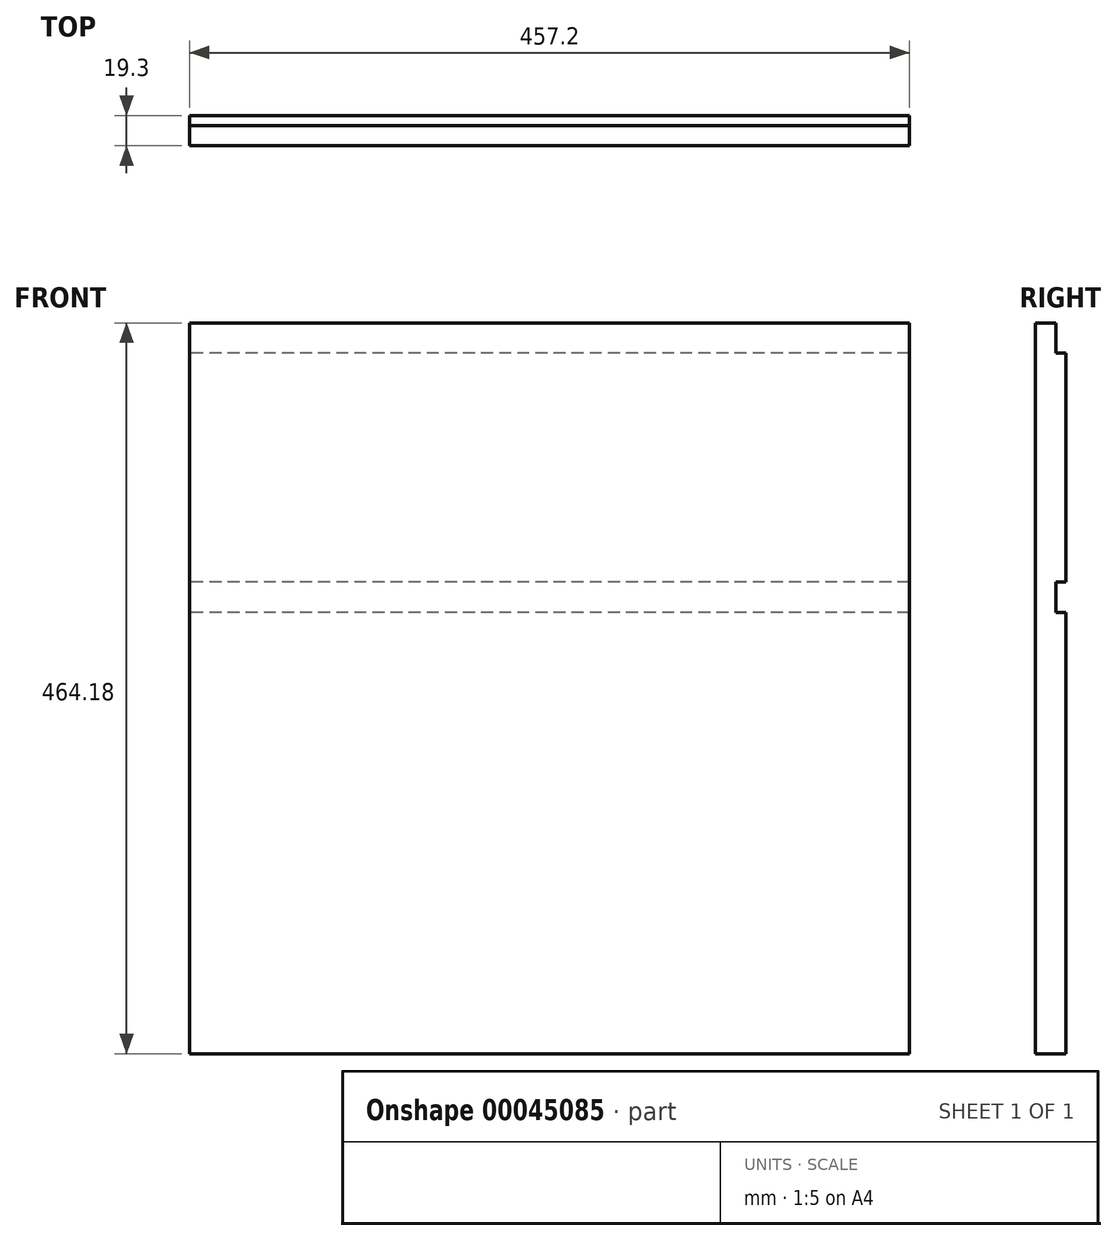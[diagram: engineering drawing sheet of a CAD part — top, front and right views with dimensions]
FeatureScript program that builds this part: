
annotation { "Feature Type Name" : "Feature", "Feature Type Description" : "" }
export const myFeature = defineFeature(function(context is Context, id is Id, definition is map)
    precondition{}
    {
        {
            var Q0;
            Q0=qCreatedBy(makeId("Front.planeOp"),FACE);
            var sketch = newSketch(context, id + "F0", { "sketchPlane" : qUnion([Q0])});
            skLineSegment(sketch, "E0.rect.bottom", {"start": v(-228.6, 232.1) * mm, "end": v(228.6, 232.1) * mm});
            skLineSegment(sketch, "E0.rect.top", {"start": v(-228.6, -232.1) * mm, "end": v(228.6, -232.1) * mm});
            skLineSegment(sketch, "E0.rect.left", {"start": v(-228.6, 232.1) * mm, "end": v(-228.6, -232.1) * mm});
            skLineSegment(sketch, "E0.rect.right", {"start": v(228.6, 232.1) * mm, "end": v(228.6, -232.1) * mm});
            skPoint(sketch, "E0.rect.middle", {"position": v(0, 0) * mm});
            skSolve(sketch);
        }
        {
            var Q0;
            Q0 = qSketchRegion(id + "F0", true);
            extrude(context, id + "F1", {"entities" : qUnion([Q0]), "depth" : 19.3 * mm});
        }
        {
            var Q0;
            Q0=makeQuery(id+"F1.opExtrude","CAP_FACE",FACE,{"disambiguationData":[OSD([sQuery(id+"F0.wireOp",EDGE,"E0.rect.bottom"),sQuery(id+"F0.wireOp",EDGE,"E0.rect.top"),sQuery(id+"F0.wireOp",EDGE,"E0.rect.left"),sQuery(id+"F0.wireOp",EDGE,"E0.rect.right")])],"isStart":true});
            var sketch = newSketch(context, id + "F2", { "sketchPlane" : qUnion([Q0])});
            skLineSegment(sketch, "E1.bottom", {"start": v(-228.6, 232.1) * mm, "end": v(228.6, 232.1) * mm});
            skLineSegment(sketch, "E1.top", {"start": v(-228.6, 212.79) * mm, "end": v(228.6, 212.79) * mm});
            skLineSegment(sketch, "E1.left", {"start": v(-228.6, 232.1) * mm, "end": v(-228.6, 212.79) * mm});
            skLineSegment(sketch, "E1.right", {"start": v(228.6, 232.1) * mm, "end": v(228.6, 212.79) * mm});
            skLineSegment(sketch, "E2.bottom", {"start": v(-228.6, 67.37) * mm, "end": v(228.6, 67.37) * mm});
            skLineSegment(sketch, "E2.top", {"start": v(-228.6, 48.07) * mm, "end": v(228.6, 48.07) * mm});
            skLineSegment(sketch, "E2.left", {"start": v(-228.6, 67.37) * mm, "end": v(-228.6, 48.07) * mm});
            skLineSegment(sketch, "E2.right", {"start": v(228.6, 67.37) * mm, "end": v(228.6, 48.07) * mm});
            skSolve(sketch);
        }
        {
            var Q0;
            Q0 = qSketchRegion(id + "F2", true);
            extrude(context, id + "F3", {"entities" : qUnion([Q0]), "operationType" : NewBodyOperationType.REMOVE, "oppositeDirection" : true, "depth" : 6.35 * mm});
        }
    });
